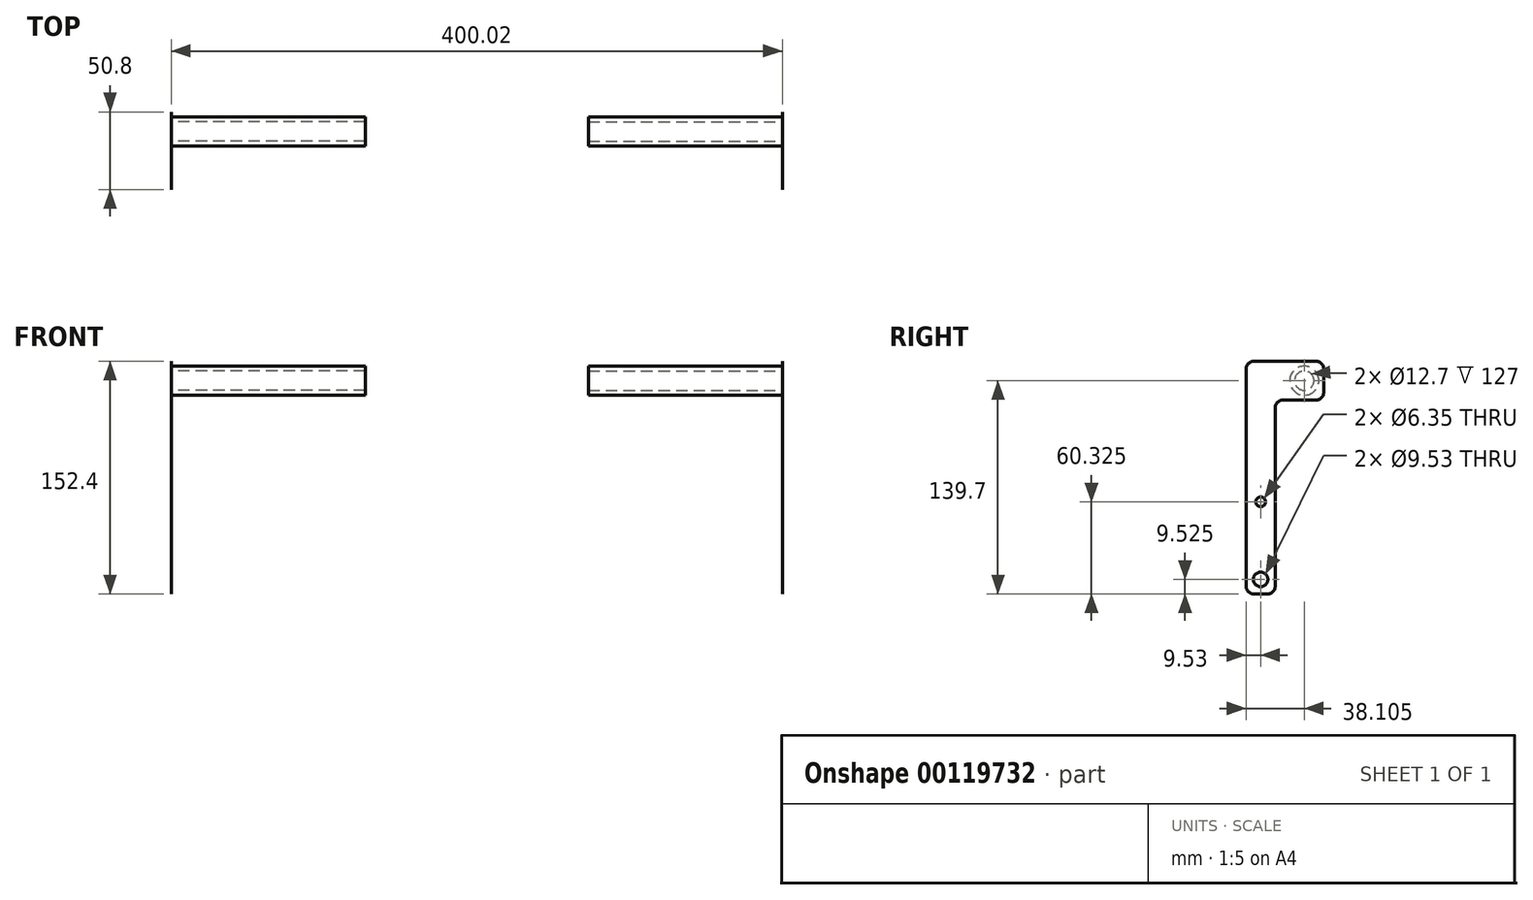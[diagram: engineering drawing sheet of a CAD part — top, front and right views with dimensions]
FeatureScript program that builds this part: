
annotation { "Feature Type Name" : "Feature", "Feature Type Description" : "" }
export const myFeature = defineFeature(function(context is Context, id is Id, definition is map)
    precondition{}
    {
        {
            var Q0;
            Q0=qCreatedBy(makeId("Right.planeOp"),FACE);
            var sketch = newSketch(context, id + "F0", { "sketchPlane" : qUnion([Q0])});
            skLineSegment(sketch, "E0.bottom", {"start": v(-9.52, 0) * mm, "end": v(9.52, 0) * mm});
            skLineSegment(sketch, "E0.top", {"start": v(-9.53, 152.4) * mm, "end": v(9.53, 152.4) * mm});
            skLineSegment(sketch, "E0.left", {"start": v(-9.52, 0) * mm, "end": v(-9.53, 152.4) * mm});
            skLineSegment(sketch, "E0.right", {"start": v(9.53, 0) * mm, "end": v(9.52, 152.4) * mm});
            skLineSegment(sketch, "E1.bottom", {"start": v(9.53, 152.4) * mm, "end": v(41.27, 152.4) * mm});
            skLineSegment(sketch, "E1.top", {"start": v(9.52, 127) * mm, "end": v(41.27, 127) * mm});
            skLineSegment(sketch, "E1.left", {"start": v(9.53, 152.4) * mm, "end": v(9.53, 127) * mm});
            skLineSegment(sketch, "E1.right", {"start": v(41.27, 152.4) * mm, "end": v(41.27, 127) * mm});
            skSolve(sketch);
        }
        {
            var Q0;
            Q0=qSketchRegion(id+"F0",true);
            extrude(context, id + "F1", {"entities" : qUnion([Q0]), "oppositeDirection" : true, "depth" : 1 / 101.6 * mm});
        }
        {
            var Q0;
            Q0=makeQuery(id+"F1.opExtrude","CAP_FACE",FACE,{"disambiguationData":[OSD([sQuery(id+"F0.wireOp",EDGE,"E0.bottom"),sQuery(id+"F0.wireOp",EDGE,"E0.top"),sQuery(id+"F0.wireOp",EDGE,"E0.left"),sQuery(id+"F0.wireOp",EDGE,"E0.right"),sQuery(id+"F0.wireOp",EDGE,"E1.bottom"),sQuery(id+"F0.wireOp",EDGE,"E1.top"),sQuery(id+"F0.wireOp",EDGE,"E1.right")])],"isStart":true});
            var sketch = newSketch(context, id + "F2", { "sketchPlane" : qUnion([Q0])});
            skCircle(sketch, "E2", {"center": v(28.57, 139.7) * mm, "radius": 9.53 * mm});
            skPoint(sketch, "E2.centerSnap0", {"position": v(41.27, 139.7) * mm});
            skCircle(sketch, "E3", {"center": v(28.57, 139.7) * mm, "radius": 6.35 * mm});
            skSolve(sketch);
        }
        {
            var Q0;
            Q0=qSketchRegion(id+"F2",true);
            extrude(context, id + "F3", {"entities" : qUnion([Q0]), "operationType" : NewBodyOperationType.ADD, "depth" : 127 * mm});
        }
        {
            var Q0;
            Q0=makeQuery(id+"F1.opExtrude","SWEPT_EDGE",EDGE,{"disambiguationData":[OSD([sQuery(id+"F0.wireOp",EDGE,"E0.top"),sQuery(id+"F0.wireOp",EDGE,"E0.left")])]});
            var Q1;
            Q1=makeQuery(id+"F1.opExtrude","SWEPT_EDGE",EDGE,{"disambiguationData":[OSD([sQuery(id+"F0.wireOp",EDGE,"E0.right"),sQuery(id+"F0.wireOp",EDGE,"E1.top"),sQuery(id+"F0.wireOp",EDGE,"E1.left")])]});
            var Q2;
            Q2=makeQuery(id+"F1.opExtrude","SWEPT_EDGE",EDGE,{"disambiguationData":[OSD([sQuery(id+"F0.wireOp",EDGE,"E1.top"),sQuery(id+"F0.wireOp",EDGE,"E1.right")])]});
            var Q3;
            Q3=makeQuery(id+"F1.opExtrude","SWEPT_EDGE",EDGE,{"disambiguationData":[OSD([sQuery(id+"F0.wireOp",EDGE,"E1.bottom"),sQuery(id+"F0.wireOp",EDGE,"E1.right")])]});
            var Q4;
            Q4=makeQuery(id+"F1.opExtrude","SWEPT_EDGE",EDGE,{"disambiguationData":[OSD([sQuery(id+"F0.wireOp",EDGE,"E0.bottom"),sQuery(id+"F0.wireOp",EDGE,"E0.right")])]});
            var Q5;
            Q5=makeQuery(id+"F1.opExtrude","SWEPT_EDGE",EDGE,{"disambiguationData":[OSD([sQuery(id+"F0.wireOp",EDGE,"E0.bottom"),sQuery(id+"F0.wireOp",EDGE,"E0.left")])]});
            fillet(context, id + "F4", {"entities" : qUnion([Q0, Q1, Q2, Q3, Q4, Q5]), "radius" : 5 * mm, "tangentPropagation" : true, "allowEdgeOverflow" : false});
        }
        {
            var Q0;
            Q0=makeQuery(id+"F1.opExtrude","CAP_FACE",FACE,{"disambiguationData":[OSD([sQuery(id+"F0.wireOp",EDGE,"E0.bottom"),sQuery(id+"F0.wireOp",EDGE,"E0.top"),sQuery(id+"F0.wireOp",EDGE,"E0.left"),sQuery(id+"F0.wireOp",EDGE,"E0.right"),sQuery(id+"F0.wireOp",EDGE,"E1.bottom"),sQuery(id+"F0.wireOp",EDGE,"E1.top"),sQuery(id+"F0.wireOp",EDGE,"E1.right")])],"isStart":true});
            var sketch = newSketch(context, id + "F5", { "sketchPlane" : qUnion([Q0])});
            skCircle(sketch, "E4", {"center": v(0, 9.53) * mm, "radius": 4.76 * mm});
            skCircle(sketch, "E5", {"center": v(0, 60.33) * mm, "radius": 3.18 * mm});
            skSolve(sketch);
        }
        {
            var Q0;
            Q0=qSketchRegion(id+"F5",true);
            extrude(context, id + "F6", {"entities" : qUnion([Q0]), "operationType" : NewBodyOperationType.REMOVE, "endBound" : BoundingType.THROUGH_ALL, "oppositeDirection" : true, "depth" : 25 * mm});
        }
        {
            var Q0;
            Q0=qCreatedBy(makeId("Right.planeOp"),FACE);
            cPlane(context, id + "F7", {"entities" : qUnion([Q0]), "cplaneType" : CPlaneType.OFFSET, "offset" : 200 * mm, "width" : 150 * mm, "height" : 150 * mm});
        }
        {
            var Q0;
            Q0=makeQuery(id+"F1.opExtrude","SWEPT_BODY",BODY,{"disambiguationData":[OSD([sQuery(id+"F0.wireOp",EDGE,"E0.bottom"),sQuery(id+"F0.wireOp",EDGE,"E0.top"),sQuery(id+"F0.wireOp",EDGE,"E0.left"),sQuery(id+"F0.wireOp",EDGE,"E0.right"),sQuery(id+"F0.wireOp",EDGE,"E1.bottom"),sQuery(id+"F0.wireOp",EDGE,"E1.top"),sQuery(id+"F0.wireOp",EDGE,"E1.right")])]});
            var Q1;
            Q1=qCreatedBy(id+"F7.planeOp",FACE);
            mirror(context, id + "F8", {"entities" : qUnion([Q0]), "mirrorPlane" : qUnion([Q1])});
        }
    });
